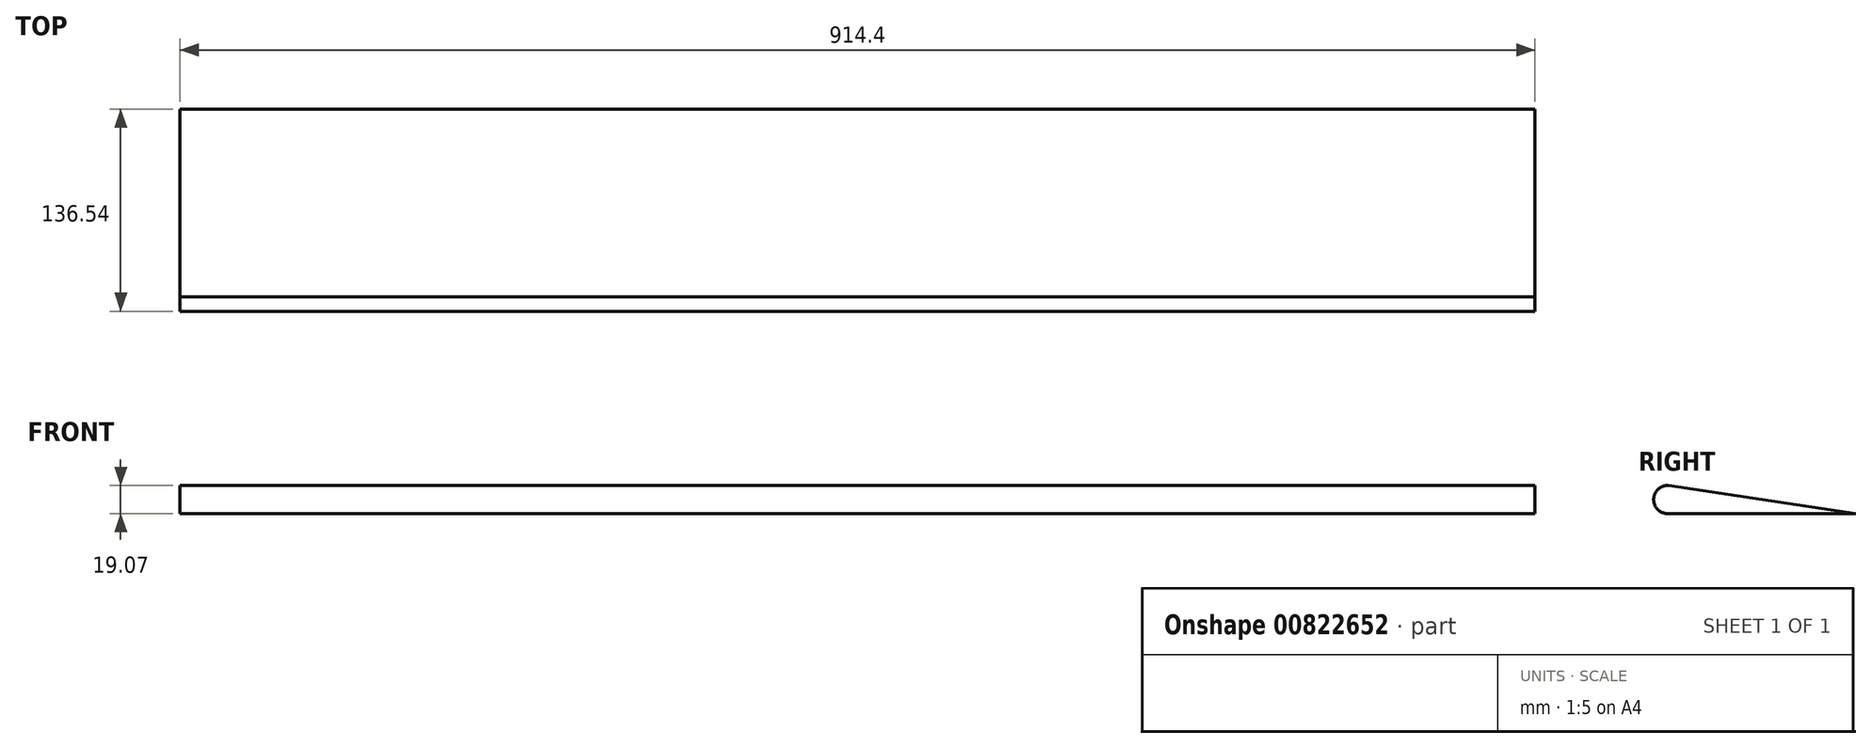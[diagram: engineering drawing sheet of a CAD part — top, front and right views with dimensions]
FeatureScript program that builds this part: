
annotation { "Feature Type Name" : "Feature", "Feature Type Description" : "" }
export const myFeature = defineFeature(function(context is Context, id is Id, definition is map)
    precondition{}
    {
        {
            var Q0;
            Q0=qCreatedBy(makeId("Right.planeOp"),FACE);
            var sketch = newSketch(context, id + "F0", { "sketchPlane" : qUnion([Q0])});
            skLineSegment(sketch, "E0", {"start": v(-54.11, 0) * mm, "end": v(72.89, 0) * mm});
            skArc(sketch, "E1", {"start": v(-54.11, 0) * mm, "mid": v(-63.65, 9.73) * mm, "end": v(-53.72, 19.06) * mm});
            skLineSegment(sketch, "E2", {"start": v(-53.72, 19.06) * mm, "end": v(72.89, 0) * mm});
            skSolve(sketch);
        }
        {
            var Q0;
            Q0 = qSketchRegion(id + "F0", true);
            extrude(context, id + "F1", {"entities" : qUnion([Q0]), "endBound" : BoundingType.SYMMETRIC, "depth" : 914.4 * mm, "offsetDistance" : 25.4 * mm});
        }
    });
